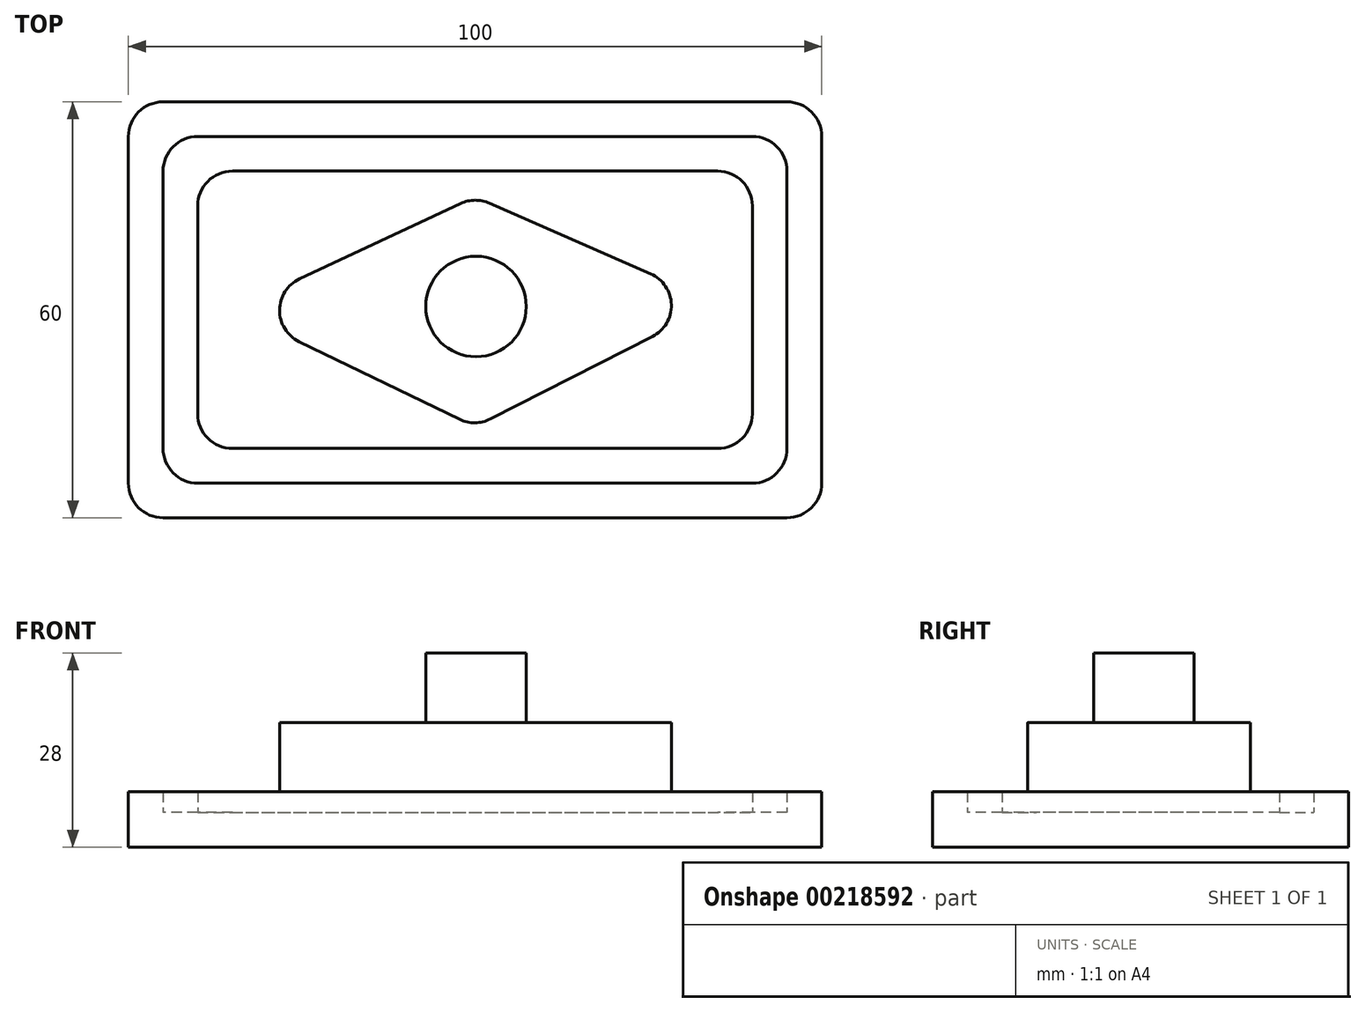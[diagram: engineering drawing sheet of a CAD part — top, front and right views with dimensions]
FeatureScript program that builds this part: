
annotation { "Feature Type Name" : "Feature", "Feature Type Description" : "" }
export const myFeature = defineFeature(function(context is Context, id is Id, definition is map)
    precondition{}
    {
        {
            var Q0;
            Q0=qCreatedBy(makeId("Top.planeOp"),FACE);
            var sketch = newSketch(context, id + "F0", { "sketchPlane" : qUnion([Q0])});
            skLineSegment(sketch, "E0.bottom", {"start": v(-40.28, 35.5) * mm, "end": v(59.72, 35.5) * mm});
            skLineSegment(sketch, "E0.top", {"start": v(-40.28, -24.5) * mm, "end": v(59.72, -24.5) * mm});
            skLineSegment(sketch, "E0.left", {"start": v(-40.28, 35.5) * mm, "end": v(-40.28, -24.5) * mm});
            skLineSegment(sketch, "E0.right", {"start": v(59.72, 35.5) * mm, "end": v(59.72, -24.5) * mm});
            skLineSegment(sketch, "E1.0", {"start": v(-35.28, 30.5) * mm, "end": v(54.72, 30.5) * mm});
            skLineSegment(sketch, "E1.1", {"start": v(-35.28, 30.5) * mm, "end": v(-35.28, -19.5) * mm});
            skLineSegment(sketch, "E1.2", {"start": v(-35.28, -19.5) * mm, "end": v(54.72, -19.5) * mm});
            skLineSegment(sketch, "E1.3", {"start": v(54.72, 30.5) * mm, "end": v(54.72, -19.5) * mm});
            skLineSegment(sketch, "E2.0", {"start": v(-30.28, 25.5) * mm, "end": v(49.72, 25.5) * mm});
            skLineSegment(sketch, "E2.1", {"start": v(-30.28, 25.5) * mm, "end": v(-30.28, -14.5) * mm});
            skLineSegment(sketch, "E2.2", {"start": v(-30.28, -14.5) * mm, "end": v(49.72, -14.5) * mm});
            skLineSegment(sketch, "E2.3", {"start": v(49.72, 25.5) * mm, "end": v(49.72, -14.5) * mm});
            skSolve(sketch);
        }
        {
            var Q0;
            Q0=makeQuery(id+"F0.imprint","IMPRINT",FACE,{"disambiguationData":[TD([[makeQuery(id+"F0.imprint","IMPRINT",EDGE,{"derivedFrom":sQuery(id+"F0.wireOp",EDGE,"E0.bottom")}),-1.0]])]});
            var Q1;
            Q1=makeQuery(id+"F0.imprint","IMPRINT",FACE,{"disambiguationData":[TD([[makeQuery(id+"F0.imprint","IMPRINT",EDGE,{"derivedFrom":sQuery(id+"F0.wireOp",EDGE,"E2.0")}),-1.0]])]});
            extrude(context, id + "F1", {"entities" : qUnion([Q0, Q1]), "depth" : 8 * mm});
        }
        {
            var Q0;
            Q0=makeQuery(id+"F0.imprint","IMPRINT",FACE,{"disambiguationData":[TD([[makeQuery(id+"F0.imprint","IMPRINT",EDGE,{"derivedFrom":sQuery(id+"F0.wireOp",EDGE,"E1.0")}),-1.0]])]});
            extrude(context, id + "F2", {"entities" : qUnion([Q0]), "operationType" : NewBodyOperationType.ADD, "depth" : 5 * mm});
        }
        {
            var Q0;
            Q0=makeQuery(id+"F1.opExtrude","CAP_FACE",FACE,{"disambiguationData":[OSD([sQuery(id+"F0.wireOp",EDGE,"E2.0"),sQuery(id+"F0.wireOp",EDGE,"E2.1"),sQuery(id+"F0.wireOp",EDGE,"E2.2"),sQuery(id+"F0.wireOp",EDGE,"E2.3")])],"isStart":false});
            var sketch = newSketch(context, id + "F3", { "sketchPlane" : qUnion([Q0])});
            skLineSegment(sketch, "E3", {"start": v(-25.1, 5.5) * mm, "end": v(9.72, -11.38) * mm});
            skPoint(sketch, "E3.startSnap0", {"position": v(-30.28, 5.5) * mm});
            skPoint(sketch, "E3.endSnap0", {"position": v(9.72, -14.5) * mm});
            skLineSegment(sketch, "E4", {"start": v(9.72, -11.38) * mm, "end": v(44.72, 6.43) * mm});
            skLineSegment(sketch, "E5", {"start": v(44.72, 6.43) * mm, "end": v(9.72, 21.8) * mm});
            skLineSegment(sketch, "E6", {"start": v(9.72, 21.8) * mm, "end": v(-25.1, 5.5) * mm});
            skSolve(sketch);
        }
        {
            var Q0;
            Q0=makeQuery(id+"F3.imprint","IMPRINT",FACE,{"disambiguationData":[TD([[makeQuery(id+"F3.imprint","IMPRINT",EDGE,{"derivedFrom":sQuery(id+"F3.wireOp",EDGE,"E3")}),1.0]])]});
            extrude(context, id + "F4", {"entities" : qUnion([Q0]), "operationType" : NewBodyOperationType.ADD, "depth" : 10 * mm});
        }
        {
            var Q0;
            Q0=makeQuery(id+"F1.opExtrude","SWEPT_EDGE",EDGE,{"disambiguationData":[OSD([sQuery(id+"F0.wireOp",EDGE,"E1.2"),sQuery(id+"F0.wireOp",EDGE,"E1.3")])]});
            var Q1;
            Q1=makeQuery(id+"F1.opExtrude","SWEPT_EDGE",EDGE,{"disambiguationData":[OSD([sQuery(id+"F0.wireOp",EDGE,"E1.1"),sQuery(id+"F0.wireOp",EDGE,"E1.2")])]});
            var Q2;
            Q2=makeQuery(id+"F1.opExtrude","SWEPT_EDGE",EDGE,{"disambiguationData":[OSD([sQuery(id+"F0.wireOp",EDGE,"E1.0"),sQuery(id+"F0.wireOp",EDGE,"E1.1")])]});
            var Q3;
            Q3=makeQuery(id+"F1.opExtrude","SWEPT_EDGE",EDGE,{"disambiguationData":[OSD([sQuery(id+"F0.wireOp",EDGE,"E1.0"),sQuery(id+"F0.wireOp",EDGE,"E1.3")])]});
            var Q4;
            Q4=makeQuery(id+"F1.opExtrude","SWEPT_EDGE",EDGE,{"disambiguationData":[OSD([sQuery(id+"F0.wireOp",EDGE,"E2.0"),sQuery(id+"F0.wireOp",EDGE,"E2.1")])]});
            var Q5;
            Q5=makeQuery(id+"F1.opExtrude","SWEPT_EDGE",EDGE,{"disambiguationData":[OSD([sQuery(id+"F0.wireOp",EDGE,"E2.1"),sQuery(id+"F0.wireOp",EDGE,"E2.2")])]});
            var Q6;
            Q6=makeQuery(id+"F1.opExtrude","SWEPT_EDGE",EDGE,{"disambiguationData":[OSD([sQuery(id+"F0.wireOp",EDGE,"E2.2"),sQuery(id+"F0.wireOp",EDGE,"E2.3")])]});
            var Q7;
            Q7=makeQuery(id+"F1.opExtrude","SWEPT_EDGE",EDGE,{"disambiguationData":[OSD([sQuery(id+"F0.wireOp",EDGE,"E2.0"),sQuery(id+"F0.wireOp",EDGE,"E2.3")])]});
            var Q8;
            Q8=makeQuery(id+"F4.opExtrude","SWEPT_EDGE",EDGE,{"disambiguationData":[OSD([sQuery(id+"F3.wireOp",EDGE,"E4"),sQuery(id+"F3.wireOp",EDGE,"E5")])]});
            var Q9;
            Q9=makeQuery(id+"F4.opExtrude","SWEPT_EDGE",EDGE,{"disambiguationData":[OSD([sQuery(id+"F3.wireOp",EDGE,"E5"),sQuery(id+"F3.wireOp",EDGE,"E6")])]});
            var Q10;
            Q10=makeQuery(id+"F4.opExtrude","SWEPT_EDGE",EDGE,{"disambiguationData":[OSD([sQuery(id+"F3.wireOp",EDGE,"E3"),sQuery(id+"F3.wireOp",EDGE,"E4")])]});
            var Q11;
            Q11=makeQuery(id+"F4.opExtrude","SWEPT_EDGE",EDGE,{"disambiguationData":[OSD([sQuery(id+"F3.wireOp",EDGE,"E3"),sQuery(id+"F3.wireOp",EDGE,"E6")])]});
            fillet(context, id + "F5", {"entities" : qUnion([Q0, Q1, Q2, Q3, Q4, Q5, Q6, Q7, Q8, Q9, Q10, Q11]), "radius" : 5 * mm, "tangentPropagation" : true, "allowEdgeOverflow" : false});
        }
        {
            var Q0;
            Q0=makeQuery(id+"F4.opExtrude","CAP_FACE",FACE,{"disambiguationData":[OSD([sQuery(id+"F3.wireOp",EDGE,"E3"),sQuery(id+"F3.wireOp",EDGE,"E4"),sQuery(id+"F3.wireOp",EDGE,"E5"),sQuery(id+"F3.wireOp",EDGE,"E6")])],"isStart":false});
            var sketch = newSketch(context, id + "F6", { "sketchPlane" : qUnion([Q0])});
            skCircle(sketch, "E7", {"center": v(9.86, 5.97) * mm, "radius": 7.24 * mm});
            skSolve(sketch);
        }
        {
            var Q0;
            Q0=makeQuery(id+"F6.imprint","IMPRINT",FACE,{"disambiguationData":[TD([[makeQuery(id+"F6.imprint","IMPRINT",EDGE,{"derivedFrom":sQuery(id+"F6.wireOp",EDGE,"E7")}),1.0]])]});
            extrude(context, id + "F7", {"entities" : qUnion([Q0]), "operationType" : NewBodyOperationType.ADD, "depth" : 10 * mm});
        }
        {
            var Q0;
            Q0=makeQuery(id+"F1.opExtrude","SWEPT_EDGE",EDGE,{"disambiguationData":[OSD([sQuery(id+"F0.wireOp",EDGE,"E0.top"),sQuery(id+"F0.wireOp",EDGE,"E0.right")])]});
            var Q1;
            Q1=makeQuery(id+"F1.opExtrude","SWEPT_EDGE",EDGE,{"disambiguationData":[OSD([sQuery(id+"F0.wireOp",EDGE,"E0.top"),sQuery(id+"F0.wireOp",EDGE,"E0.left")])]});
            var Q2;
            Q2=makeQuery(id+"F1.opExtrude","SWEPT_EDGE",EDGE,{"disambiguationData":[OSD([sQuery(id+"F0.wireOp",EDGE,"E0.bottom"),sQuery(id+"F0.wireOp",EDGE,"E0.left")])]});
            var Q3;
            Q3=makeQuery(id+"F1.opExtrude","SWEPT_EDGE",EDGE,{"disambiguationData":[OSD([sQuery(id+"F0.wireOp",EDGE,"E0.bottom"),sQuery(id+"F0.wireOp",EDGE,"E0.right")])]});
            fillet(context, id + "F8", {"entities" : qUnion([Q0, Q1, Q2, Q3]), "radius" : 5 * mm, "tangentPropagation" : true, "allowEdgeOverflow" : false});
        }
    });
